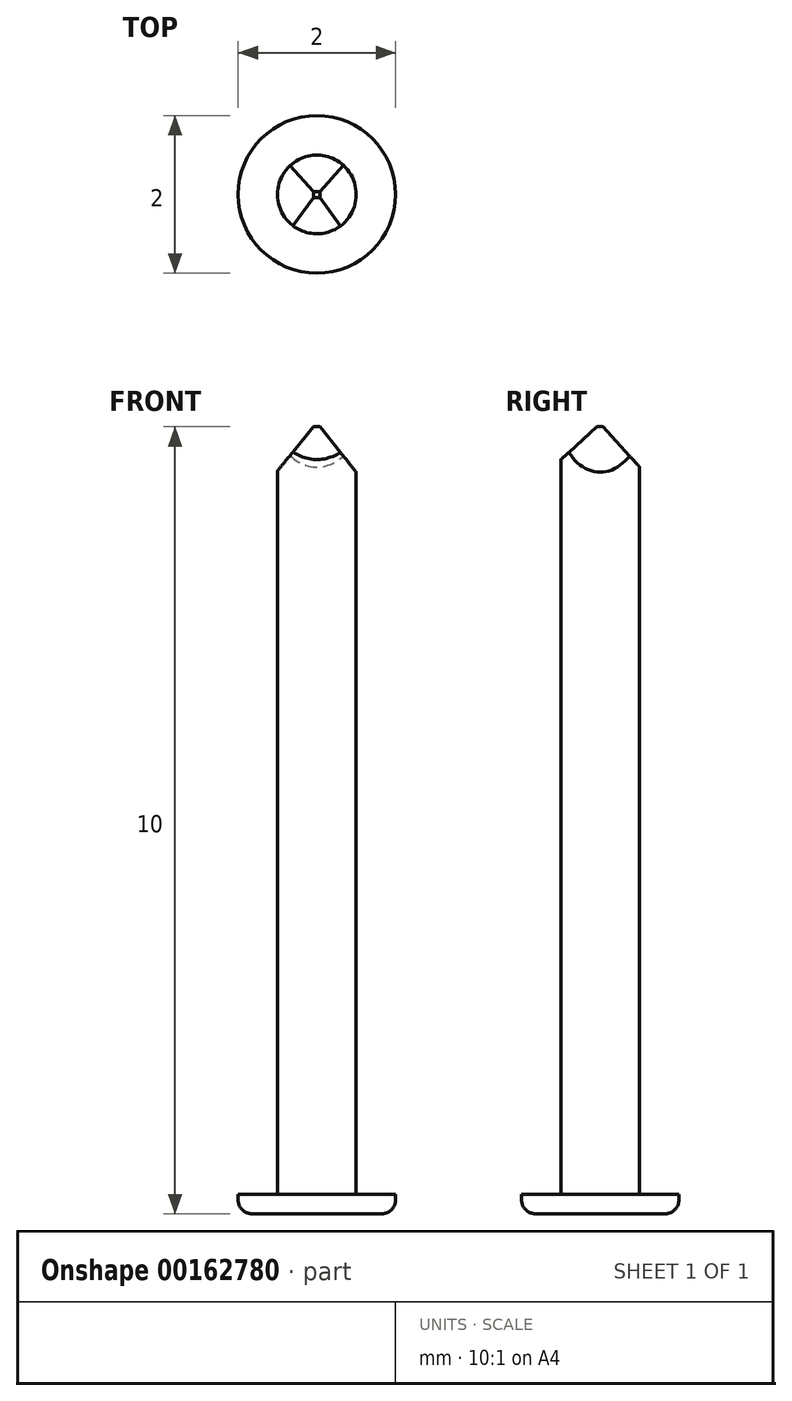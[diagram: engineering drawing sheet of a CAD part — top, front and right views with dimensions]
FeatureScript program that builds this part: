
annotation { "Feature Type Name" : "Feature", "Feature Type Description" : "" }
export const myFeature = defineFeature(function(context is Context, id is Id, definition is map)
    precondition{}
    {
        {
            var Q0;
            Q0=qCreatedBy(makeId("Top.planeOp"),FACE);
            var sketch = newSketch(context, id + "F0", { "sketchPlane" : qUnion([Q0])});
            skCircle(sketch, "E0", {"center": v(0, 0) * mm, "radius": 1 * mm});
            skCircle(sketch, "E1", {"center": v(0, 0) * mm, "radius": 0.5 * mm});
            skSolve(sketch);
        }
        {
            var Q0;
            Q0=makeQuery(id+"F0.imprint","IMPRINT",FACE,{"disambiguationData":[TD([[makeQuery(id+"F0.imprint","IMPRINT",EDGE,{"derivedFrom":sQuery(id+"F0.wireOp",EDGE,"E1")}),1.0]])]});
            extrude(context, id + "F1", {"entities" : qUnion([Q0]), "depth" : 10 * mm});
        }
        {
            var Q0;
            Q0 = qSketchRegion(id + "F0", true);
            extrude(context, id + "F2", {"entities" : qUnion([Q0]), "operationType" : NewBodyOperationType.ADD, "depth" : 0.25 * mm});
        }
        {
            var Q0;
            Q0=makeQuery(id+"F2.opExtrude","CAP_EDGE",EDGE,{"disambiguationData":[OSD([sQuery(id+"F0.wireOp",EDGE,"E0")])],"isStart":true});
            fillet(context, id + "F3", {"entities" : qUnion([Q0]), "radius" : 0.18 * mm, "tangentPropagation" : true, "allowEdgeOverflow" : false});
        }
        {
            var Q0;
            Q0=qCreatedBy(makeId("Front.planeOp"),FACE);
            var sketch = newSketch(context, id + "F4", { "sketchPlane" : qUnion([Q0])});
            skLineSegment(sketch, "E2", {"start": v(-0.72, 9.17) * mm, "end": v(0, 10.05) * mm});
            skLineSegment(sketch, "E3", {"start": v(0, 10.05) * mm, "end": v(0.72, 9.15) * mm});
            skLineSegment(sketch, "E4", {"start": v(0.72, 9.15) * mm, "end": v(1.92, 9.15) * mm});
            skLineSegment(sketch, "E5", {"start": v(1.92, 9.15) * mm, "end": v(1.92, 11.25) * mm});
            skLineSegment(sketch, "E6", {"start": v(1.92, 11.25) * mm, "end": v(-1.57, 11.25) * mm});
            skLineSegment(sketch, "E7", {"start": v(-1.57, 11.25) * mm, "end": v(-1.57, 9.13) * mm});
            skLineSegment(sketch, "E8", {"start": v(-1.57, 9.13) * mm, "end": v(-0.72, 9.17) * mm});
            skSolve(sketch);
        }
        {
            var Q0;
            Q0 = qSketchRegion(id + "F4", true);
            extrude(context, id + "F5", {"entities" : qUnion([Q0]), "operationType" : NewBodyOperationType.REMOVE, "oppositeDirection" : true, "depth" : 50 * mm, "hasSecondDirection" : true, "secondDirectionOppositeDirection" : false, "secondDirectionDepth" : 2.6 * mm});
        }
        {
            var Q0;
            Q0=qCreatedBy(makeId("Right.planeOp"),FACE);
            var sketch = newSketch(context, id + "F6", { "sketchPlane" : qUnion([Q0])});
            skLineSegment(sketch, "E9", {"start": v(-0.7, 9.4) * mm, "end": v(0, 10.04) * mm});
            skLineSegment(sketch, "E10", {"start": v(0, 10.04) * mm, "end": v(0.62, 9.36) * mm});
            skLineSegment(sketch, "E11", {"start": v(0.62, 9.36) * mm, "end": v(1.56, 9.36) * mm});
            skLineSegment(sketch, "E12", {"start": v(1.56, 9.36) * mm, "end": v(1.56, 11) * mm});
            skLineSegment(sketch, "E13", {"start": v(1.56, 11) * mm, "end": v(-1.62, 11) * mm});
            skLineSegment(sketch, "E14", {"start": v(-1.62, 11) * mm, "end": v(-1.62, 9.46) * mm});
            skLineSegment(sketch, "E15", {"start": v(-1.62, 9.46) * mm, "end": v(-0.7, 9.4) * mm});
            skSolve(sketch);
        }
        {
            var Q0;
            Q0 = qSketchRegion(id + "F6", true);
            extrude(context, id + "F7", {"entities" : qUnion([Q0]), "operationType" : NewBodyOperationType.REMOVE, "oppositeDirection" : true, "depth" : 50 * mm, "hasSecondDirection" : true, "secondDirectionOppositeDirection" : false, "secondDirectionDepth" : 2.88 * mm});
        }
    });
